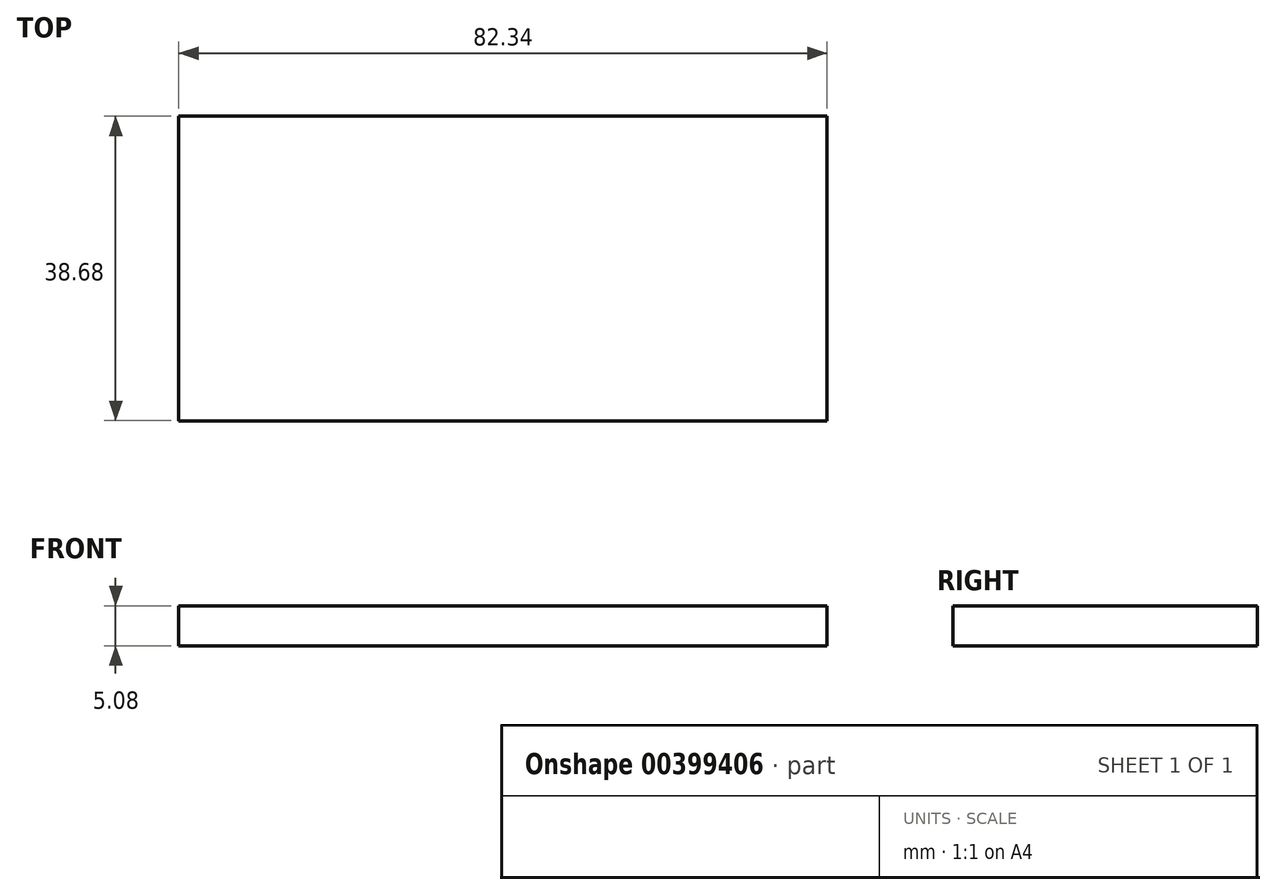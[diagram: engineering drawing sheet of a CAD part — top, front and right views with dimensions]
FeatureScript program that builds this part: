
annotation { "Feature Type Name" : "Feature", "Feature Type Description" : "" }
export const myFeature = defineFeature(function(context is Context, id is Id, definition is map)
    precondition{}
    {
        {
            var Q0;
            Q0=qCreatedBy(makeId("Top.planeOp"),FACE);
            var sketch = newSketch(context, id + "F0", { "sketchPlane" : qUnion([Q0])});
            skLineSegment(sketch, "E0.bottom", {"start": v(-41.17, 19.34) * mm, "end": v(41.17, 19.34) * mm});
            skLineSegment(sketch, "E0.top", {"start": v(-41.17, -19.34) * mm, "end": v(41.17, -19.34) * mm});
            skLineSegment(sketch, "E0.left", {"start": v(-41.17, 19.34) * mm, "end": v(-41.17, -19.34) * mm});
            skLineSegment(sketch, "E0.right", {"start": v(41.17, 19.34) * mm, "end": v(41.17, -19.34) * mm});
            skPoint(sketch, "E0.middle", {"position": v(0, 0) * mm});
            skSolve(sketch);
        }
        {
            var Q0;
            Q0=makeQuery(id+"F0.imprint","IMPRINT",FACE,{"disambiguationData":[TD([[makeQuery(id+"F0.imprint","IMPRINT",EDGE,{"derivedFrom":sQuery(id+"F0.wireOp",EDGE,"E0.bottom")}),-1.0]])]});
            extrude(context, id + "F1", {"entities" : qUnion([Q0]), "depth" : 5.08 * mm});
        }
    });
